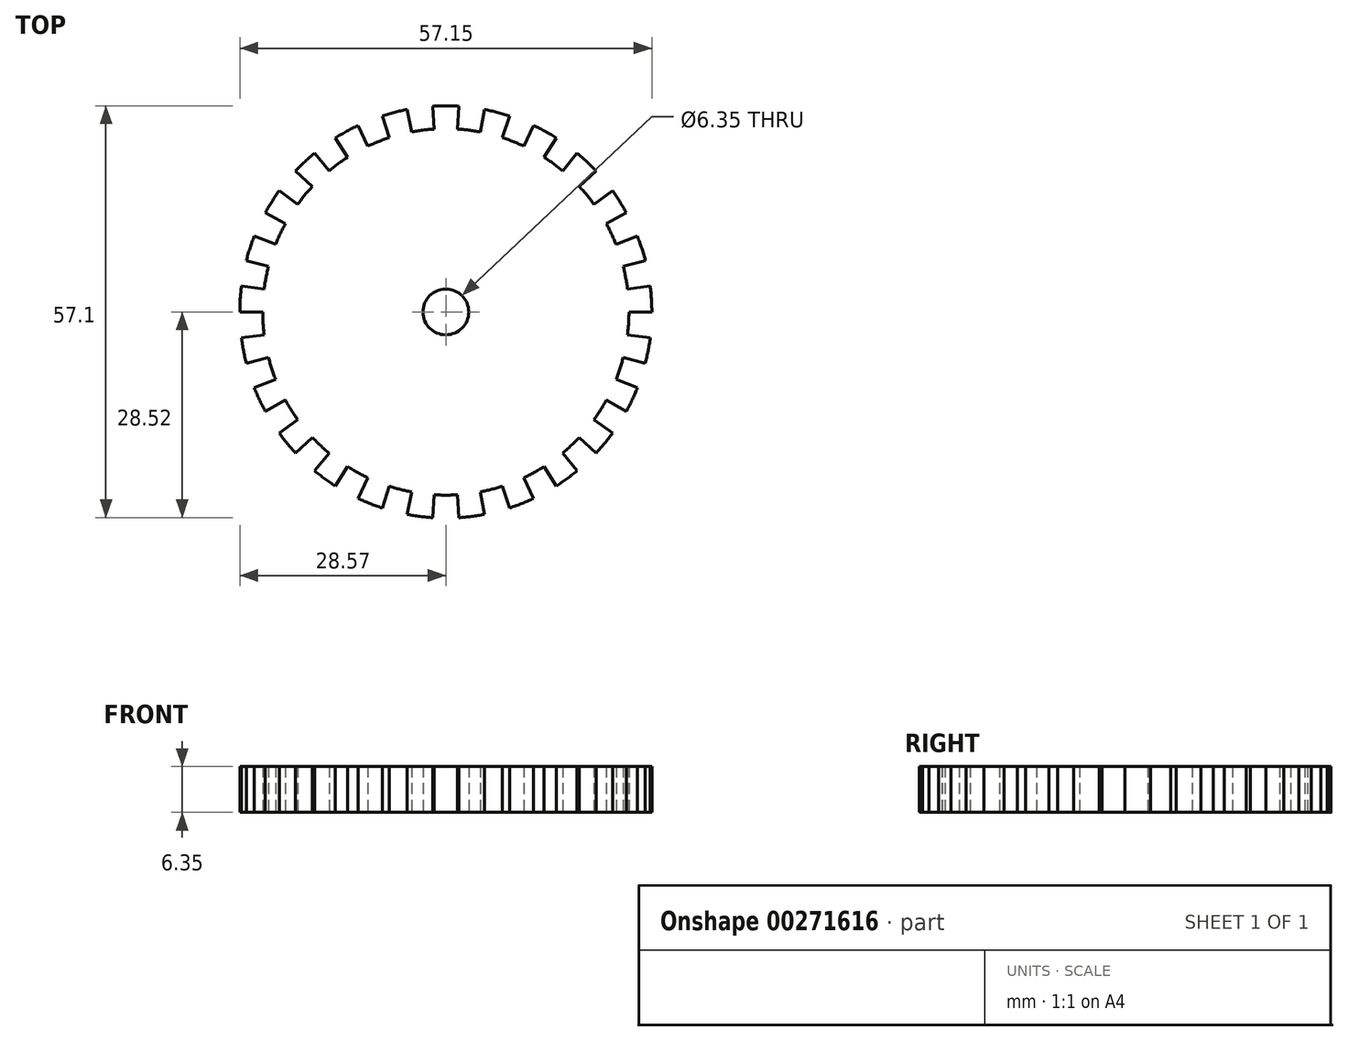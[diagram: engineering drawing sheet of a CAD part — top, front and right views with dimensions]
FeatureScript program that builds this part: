
annotation { "Feature Type Name" : "Feature", "Feature Type Description" : "" }
export const myFeature = defineFeature(function(context is Context, id is Id, definition is map)
    precondition{}
    {
        {
            var Q0;
            Q0=qCreatedBy(makeId("Top.planeOp"),FACE);
            var sketch = newSketch(context, id + "F0", { "sketchPlane" : qUnion([Q0])});
            skArc(sketch, "E0", {"start": v(-5.35, 28.07) * mm, "mid": v(-7.1, 27.68) * mm, "end": v(-8.83, 27.18) * mm});
            skArc(sketch, "E1", {"start": v(-1.6, 25.35) * mm, "mid": v(-3.18, 25.2) * mm, "end": v(-4.76, 24.95) * mm});
            skLineSegment(sketch, "E2", {"start": v(22.26, 12.24) * mm, "end": v(25.04, 13.77) * mm});
            skLineSegment(sketch, "E3", {"start": v(24.6, -6.32) * mm, "end": v(27.68, -7.1) * mm});
            skLineSegment(sketch, "E4", {"start": v(22.26, -12.24) * mm, "end": v(25.04, -13.77) * mm});
            skLineSegment(sketch, "E5", {"start": v(18.52, -17.39) * mm, "end": v(20.83, -19.56) * mm});
            skLineSegment(sketch, "E6.trimOffspring", {"start": v(1.8, -28.52) * mm, "end": v(1.6, -25.35) * mm});
            skLineSegment(sketch, "E7.trimOffspring", {"start": v(5.35, -28.07) * mm, "end": v(4.76, -24.95) * mm});
            skLineSegment(sketch, "E8.trimOffspring", {"start": v(8.83, -27.18) * mm, "end": v(7.85, -24.16) * mm});
            skLineSegment(sketch, "E9.trimOffspring", {"start": v(12.17, -25.86) * mm, "end": v(10.81, -22.98) * mm});
            skLineSegment(sketch, "E10.trimOffspring", {"start": v(15.31, -24.13) * mm, "end": v(13.61, -21.45) * mm});
            skLineSegment(sketch, "E11.trimOffspring", {"start": v(18.21, -22.02) * mm, "end": v(16.2, -19.57) * mm});
            skLineSegment(sketch, "E12.trimOffspring", {"start": v(23.12, -16.8) * mm, "end": v(20.55, -14.93) * mm});
            skLineSegment(sketch, "E13.trimOffspring", {"start": v(26.57, -10.52) * mm, "end": v(23.62, -9.35) * mm});
            skLineSegment(sketch, "E14.trimOffspring", {"start": v(28.35, -3.58) * mm, "end": v(25.2, -3.18) * mm});
            skLineSegment(sketch, "E15.trimOffspring", {"start": v(28.58, 0) * mm, "end": v(25.4, 0) * mm});
            skLineSegment(sketch, "E16.trimOffspring", {"start": v(28.35, 3.58) * mm, "end": v(25.2, 3.18) * mm});
            skLineSegment(sketch, "E17.trimOffspring", {"start": v(27.68, 7.1) * mm, "end": v(24.6, 6.32) * mm});
            skLineSegment(sketch, "E18.trimOffspring", {"start": v(26.57, 10.52) * mm, "end": v(23.62, 9.35) * mm});
            skLineSegment(sketch, "E19.trimOffspring", {"start": v(23.12, 16.8) * mm, "end": v(20.55, 14.93) * mm});
            skLineSegment(sketch, "E20.trimOffspring", {"start": v(20.83, 19.56) * mm, "end": v(18.52, 17.39) * mm});
            skLineSegment(sketch, "E21.trimOffspring", {"start": v(18.21, 22.02) * mm, "end": v(16.2, 19.57) * mm});
            skLineSegment(sketch, "E22.trimOffspring", {"start": v(15.31, 24.13) * mm, "end": v(13.61, 21.45) * mm});
            skLineSegment(sketch, "E23.trimOffspring", {"start": v(12.17, 25.86) * mm, "end": v(10.81, 22.98) * mm});
            skLineSegment(sketch, "E24.trimOffspring", {"start": v(8.83, 27.18) * mm, "end": v(7.85, 24.16) * mm});
            skLineSegment(sketch, "E25.trimOffspring", {"start": v(5.35, 28.07) * mm, "end": v(4.76, 24.95) * mm});
            skLineSegment(sketch, "E26.trimOffspring", {"start": v(1.8, 28.52) * mm, "end": v(1.6, 25.35) * mm});
            skLineSegment(sketch, "E27.trimOffspring", {"start": v(-1.8, 28.52) * mm, "end": v(-1.6, 25.35) * mm});
            skLineSegment(sketch, "E28.trimOffspring", {"start": v(-5.35, 28.07) * mm, "end": v(-4.76, 24.95) * mm});
            skArc(sketch, "E29.trimOffspring", {"start": v(1.8, 28.52) * mm, "mid": v(0, 28.58) * mm, "end": v(-1.8, 28.52) * mm});
            skArc(sketch, "E30.trimOffspring", {"start": v(4.76, 24.95) * mm, "mid": v(3.18, 25.2) * mm, "end": v(1.6, 25.35) * mm});
            skArc(sketch, "E31.trimOffspring", {"start": v(8.83, 27.18) * mm, "mid": v(7.1, 27.68) * mm, "end": v(5.35, 28.07) * mm});
            skArc(sketch, "E32.trimOffspring", {"start": v(10.81, 22.98) * mm, "mid": v(9.35, 23.62) * mm, "end": v(7.85, 24.16) * mm});
            skArc(sketch, "E33.trimOffspring", {"start": v(15.31, 24.13) * mm, "mid": v(13.77, 25.04) * mm, "end": v(12.17, 25.86) * mm});
            skArc(sketch, "E34.trimOffspring", {"start": v(16.2, 19.57) * mm, "mid": v(14.93, 20.55) * mm, "end": v(13.61, 21.45) * mm});
            skArc(sketch, "E35.trimOffspring", {"start": v(20.83, 19.56) * mm, "mid": v(19.56, 20.83) * mm, "end": v(18.21, 22.02) * mm});
            skArc(sketch, "E36.trimOffspring", {"start": v(20.55, 14.93) * mm, "mid": v(19.57, 16.2) * mm, "end": v(18.52, 17.39) * mm});
            skArc(sketch, "E37.trimOffspring", {"start": v(25.04, 13.77) * mm, "mid": v(24.13, 15.31) * mm, "end": v(23.12, 16.8) * mm});
            skArc(sketch, "E38.trimOffspring", {"start": v(23.62, 9.35) * mm, "mid": v(22.98, 10.81) * mm, "end": v(22.26, 12.24) * mm});
            skArc(sketch, "E39.trimOffspring", {"start": v(27.68, 7.1) * mm, "mid": v(27.18, 8.83) * mm, "end": v(26.57, 10.52) * mm});
            skArc(sketch, "E40.trimOffspring", {"start": v(25.2, 3.18) * mm, "mid": v(24.95, 4.76) * mm, "end": v(24.6, 6.32) * mm});
            skArc(sketch, "E41.trimOffspring", {"start": v(28.58, 0) * mm, "mid": v(28.52, 1.8) * mm, "end": v(28.35, 3.58) * mm});
            skArc(sketch, "E42.trimOffspring", {"start": v(25.2, -3.18) * mm, "mid": v(25.35, -1.6) * mm, "end": v(25.4, 0) * mm});
            skArc(sketch, "E43.trimOffspring", {"start": v(27.68, -7.1) * mm, "mid": v(28.07, -5.35) * mm, "end": v(28.35, -3.58) * mm});
            skArc(sketch, "E44.trimOffspring", {"start": v(23.62, -9.35) * mm, "mid": v(24.16, -7.85) * mm, "end": v(24.6, -6.32) * mm});
            skArc(sketch, "E45.trimOffspring", {"start": v(25.04, -13.77) * mm, "mid": v(25.86, -12.17) * mm, "end": v(26.57, -10.52) * mm});
            skArc(sketch, "E46.trimOffspring", {"start": v(20.55, -14.93) * mm, "mid": v(21.45, -13.61) * mm, "end": v(22.26, -12.24) * mm});
            skArc(sketch, "E47.trimOffspring", {"start": v(20.83, -19.56) * mm, "mid": v(22.02, -18.21) * mm, "end": v(23.12, -16.8) * mm});
            skArc(sketch, "E48.trimOffspring", {"start": v(16.2, -19.57) * mm, "mid": v(17.39, -18.52) * mm, "end": v(18.52, -17.39) * mm});
            skArc(sketch, "E49.trimOffspring", {"start": v(15.31, -24.13) * mm, "mid": v(16.8, -23.12) * mm, "end": v(18.21, -22.02) * mm});
            skArc(sketch, "E50.trimOffspring", {"start": v(10.81, -22.98) * mm, "mid": v(12.24, -22.26) * mm, "end": v(13.61, -21.45) * mm});
            skArc(sketch, "E51.trimOffspring", {"start": v(8.83, -27.18) * mm, "mid": v(10.52, -26.57) * mm, "end": v(12.17, -25.86) * mm});
            skArc(sketch, "E52.trimOffspring", {"start": v(4.76, -24.95) * mm, "mid": v(6.32, -24.6) * mm, "end": v(7.85, -24.16) * mm});
            skArc(sketch, "E53.MirrorCS", {"start": v(-20.55, 14.93) * mm, "mid": v(-19.57, 16.2) * mm, "end": v(-18.52, 17.39) * mm});
            skLineSegment(sketch, "E54.MirrorCS", {"start": v(-28.35, -3.58) * mm, "end": v(-25.2, -3.18) * mm});
            skLineSegment(sketch, "E55.MirrorCS", {"start": v(-12.17, 25.86) * mm, "end": v(-10.81, 22.98) * mm});
            skLineSegment(sketch, "E56.MirrorCS", {"start": v(-23.12, -16.8) * mm, "end": v(-20.55, -14.93) * mm});
            skLineSegment(sketch, "E57.MirrorCS", {"start": v(-22.26, -12.24) * mm, "end": v(-25.04, -13.77) * mm});
            skLineSegment(sketch, "E58.MirrorCS", {"start": v(-28.58, 0) * mm, "end": v(-25.4, 0) * mm});
            skArc(sketch, "E59.MirrorCS", {"start": v(-27.68, 7.1) * mm, "mid": v(-27.18, 8.83) * mm, "end": v(-26.57, 10.52) * mm});
            skArc(sketch, "E60.MirrorCS", {"start": v(-20.55, -14.93) * mm, "mid": v(-21.45, -13.61) * mm, "end": v(-22.26, -12.24) * mm});
            skLineSegment(sketch, "E61.MirrorCS", {"start": v(-15.31, -24.13) * mm, "end": v(-13.61, -21.45) * mm});
            skLineSegment(sketch, "E62.MirrorCS", {"start": v(-5.35, -28.07) * mm, "end": v(-4.76, -24.95) * mm});
            skArc(sketch, "E63.MirrorCS", {"start": v(-16.2, -19.57) * mm, "mid": v(-17.39, -18.52) * mm, "end": v(-18.52, -17.39) * mm});
            skLineSegment(sketch, "E64.MirrorCS", {"start": v(-23.12, 16.8) * mm, "end": v(-20.55, 14.93) * mm});
            skArc(sketch, "E65.MirrorCS", {"start": v(-20.83, -19.56) * mm, "mid": v(-22.02, -18.21) * mm, "end": v(-23.12, -16.8) * mm});
            skLineSegment(sketch, "E66.MirrorCS", {"start": v(-18.21, -22.02) * mm, "end": v(-16.2, -19.57) * mm});
            skArc(sketch, "E67.MirrorCS", {"start": v(-27.68, -7.1) * mm, "mid": v(-28.07, -5.35) * mm, "end": v(-28.35, -3.58) * mm});
            skArc(sketch, "E68.MirrorCS", {"start": v(-23.62, -9.35) * mm, "mid": v(-24.16, -7.85) * mm, "end": v(-24.6, -6.32) * mm});
            skLineSegment(sketch, "E69.MirrorCS", {"start": v(-18.52, -17.39) * mm, "end": v(-20.83, -19.56) * mm});
            skArc(sketch, "E70.MirrorCS", {"start": v(-15.31, -24.13) * mm, "mid": v(-16.8, -23.12) * mm, "end": v(-18.21, -22.02) * mm});
            skLineSegment(sketch, "E71.MirrorCS", {"start": v(-27.68, 7.1) * mm, "end": v(-24.6, 6.32) * mm});
            skArc(sketch, "E72.MirrorCS", {"start": v(-25.2, 3.18) * mm, "mid": v(-24.95, 4.76) * mm, "end": v(-24.6, 6.32) * mm});
            skLineSegment(sketch, "E73.MirrorCS", {"start": v(-22.26, 12.24) * mm, "end": v(-25.04, 13.77) * mm});
            skLineSegment(sketch, "E74.MirrorCS", {"start": v(-8.83, -27.18) * mm, "end": v(-7.85, -24.16) * mm});
            skArc(sketch, "E75.MirrorCS", {"start": v(-25.2, -3.18) * mm, "mid": v(-25.35, -1.6) * mm, "end": v(-25.4, 0) * mm});
            skArc(sketch, "E76.MirrorCS", {"start": v(-20.83, 19.56) * mm, "mid": v(-19.56, 20.83) * mm, "end": v(-18.21, 22.02) * mm});
            skLineSegment(sketch, "E77.MirrorCS", {"start": v(-18.21, 22.02) * mm, "end": v(-16.2, 19.57) * mm});
            skLineSegment(sketch, "E78.MirrorCS", {"start": v(-20.83, 19.56) * mm, "end": v(-18.52, 17.39) * mm});
            skArc(sketch, "E79.MirrorCS", {"start": v(-8.83, -27.18) * mm, "mid": v(-10.52, -26.57) * mm, "end": v(-12.17, -25.86) * mm});
            skArc(sketch, "E80.MirrorCS", {"start": v(-8.83, 27.18) * mm, "mid": v(-7.1, 27.68) * mm, "end": v(-5.35, 28.07) * mm});
            skArc(sketch, "E81.MirrorCS", {"start": v(-4.76, -24.95) * mm, "mid": v(-6.32, -24.6) * mm, "end": v(-7.85, -24.16) * mm});
            skArc(sketch, "E82.MirrorCS", {"start": v(-10.81, -22.98) * mm, "mid": v(-12.24, -22.26) * mm, "end": v(-13.61, -21.45) * mm});
            skLineSegment(sketch, "E83.MirrorCS", {"start": v(-15.31, 24.13) * mm, "end": v(-13.61, 21.45) * mm});
            skLineSegment(sketch, "E84.MirrorCS", {"start": v(-26.57, 10.52) * mm, "end": v(-23.62, 9.35) * mm});
            skLineSegment(sketch, "E85.MirrorCS", {"start": v(-12.17, -25.86) * mm, "end": v(-10.81, -22.98) * mm});
            skArc(sketch, "E86.MirrorCS", {"start": v(-15.31, 24.13) * mm, "mid": v(-13.77, 25.04) * mm, "end": v(-12.17, 25.86) * mm});
            skLineSegment(sketch, "E87.MirrorCS", {"start": v(-8.83, 27.18) * mm, "end": v(-7.85, 24.16) * mm});
            skArc(sketch, "E88.MirrorCS", {"start": v(-16.2, 19.57) * mm, "mid": v(-14.93, 20.55) * mm, "end": v(-13.61, 21.45) * mm});
            skArc(sketch, "E89.MirrorCS", {"start": v(-25.04, 13.77) * mm, "mid": v(-24.13, 15.31) * mm, "end": v(-23.12, 16.8) * mm});
            skArc(sketch, "E90.MirrorCS", {"start": v(-23.62, 9.35) * mm, "mid": v(-22.98, 10.81) * mm, "end": v(-22.26, 12.24) * mm});
            skLineSegment(sketch, "E91.MirrorCS", {"start": v(-24.6, -6.32) * mm, "end": v(-27.68, -7.1) * mm});
            skArc(sketch, "E92.MirrorCS", {"start": v(-28.58, 0) * mm, "mid": v(-28.52, 1.8) * mm, "end": v(-28.35, 3.58) * mm});
            skArc(sketch, "E93.MirrorCS", {"start": v(-25.04, -13.77) * mm, "mid": v(-25.86, -12.17) * mm, "end": v(-26.57, -10.52) * mm});
            skLineSegment(sketch, "E94.MirrorCS", {"start": v(-26.57, -10.52) * mm, "end": v(-23.62, -9.35) * mm});
            skArc(sketch, "E95.MirrorCS", {"start": v(-10.81, 22.98) * mm, "mid": v(-9.35, 23.62) * mm, "end": v(-7.85, 24.16) * mm});
            skLineSegment(sketch, "E96.MirrorCS", {"start": v(-28.35, 3.58) * mm, "end": v(-25.2, 3.18) * mm});
            skLineSegment(sketch, "E97.MirrorCS", {"start": v(-1.8, -28.52) * mm, "end": v(-1.6, -25.35) * mm});
            skArc(sketch, "E98.trimOffspring", {"start": v(1.8, -28.52) * mm, "mid": v(3.58, -28.35) * mm, "end": v(5.35, -28.07) * mm});
            skArc(sketch, "E99.trimOffspring", {"start": v(-1.6, -25.35) * mm, "mid": v(0, -25.4) * mm, "end": v(1.6, -25.35) * mm});
            skArc(sketch, "E100.trimOffspring", {"start": v(-5.35, -28.07) * mm, "mid": v(-3.58, -28.35) * mm, "end": v(-1.8, -28.52) * mm});
            skArc(sketch, "E101.trimOffspring", {"start": v(-7.85, -24.16) * mm, "mid": v(-6.32, -24.6) * mm, "end": v(-4.76, -24.95) * mm});
            skArc(sketch, "E102.trimOffspring", {"start": v(-12.17, -25.86) * mm, "mid": v(-10.52, -26.57) * mm, "end": v(-8.83, -27.18) * mm});
            skArc(sketch, "E103.trimOffspring", {"start": v(-13.61, -21.45) * mm, "mid": v(-12.24, -22.26) * mm, "end": v(-10.81, -22.98) * mm});
            skArc(sketch, "E104.trimOffspring", {"start": v(-18.21, -22.02) * mm, "mid": v(-16.8, -23.12) * mm, "end": v(-15.31, -24.13) * mm});
            skArc(sketch, "E105.trimOffspring", {"start": v(-18.52, -17.39) * mm, "mid": v(-17.39, -18.52) * mm, "end": v(-16.2, -19.57) * mm});
            skArc(sketch, "E106.trimOffspring", {"start": v(-23.12, -16.8) * mm, "mid": v(-22.02, -18.21) * mm, "end": v(-20.83, -19.56) * mm});
            skArc(sketch, "E107.trimOffspring", {"start": v(-22.26, -12.24) * mm, "mid": v(-21.45, -13.61) * mm, "end": v(-20.55, -14.93) * mm});
            skArc(sketch, "E108.trimOffspring", {"start": v(-26.57, -10.52) * mm, "mid": v(-25.86, -12.17) * mm, "end": v(-25.04, -13.77) * mm});
            skArc(sketch, "E109.trimOffspring", {"start": v(-24.6, -6.32) * mm, "mid": v(-24.16, -7.85) * mm, "end": v(-23.62, -9.35) * mm});
            skArc(sketch, "E110.trimOffspring", {"start": v(-28.35, -3.58) * mm, "mid": v(-28.07, -5.35) * mm, "end": v(-27.68, -7.1) * mm});
            skArc(sketch, "E111.trimOffspring", {"start": v(-25.4, 0) * mm, "mid": v(-25.35, -1.6) * mm, "end": v(-25.2, -3.18) * mm});
            skArc(sketch, "E112.trimOffspring", {"start": v(-28.35, 3.58) * mm, "mid": v(-28.52, 1.8) * mm, "end": v(-28.58, 0) * mm});
            skArc(sketch, "E113.trimOffspring", {"start": v(-24.6, 6.32) * mm, "mid": v(-24.95, 4.76) * mm, "end": v(-25.2, 3.18) * mm});
            skArc(sketch, "E114.trimOffspring", {"start": v(-26.57, 10.52) * mm, "mid": v(-27.18, 8.83) * mm, "end": v(-27.68, 7.1) * mm});
            skArc(sketch, "E115.trimOffspring", {"start": v(-22.26, 12.24) * mm, "mid": v(-22.98, 10.81) * mm, "end": v(-23.62, 9.35) * mm});
            skArc(sketch, "E116.trimOffspring", {"start": v(-23.12, 16.8) * mm, "mid": v(-24.13, 15.31) * mm, "end": v(-25.04, 13.77) * mm});
            skArc(sketch, "E117.trimOffspring", {"start": v(-18.52, 17.39) * mm, "mid": v(-19.57, 16.2) * mm, "end": v(-20.55, 14.93) * mm});
            skArc(sketch, "E118.trimOffspring", {"start": v(-18.21, 22.02) * mm, "mid": v(-19.56, 20.83) * mm, "end": v(-20.83, 19.56) * mm});
            skArc(sketch, "E119.trimOffspring", {"start": v(-13.61, 21.45) * mm, "mid": v(-14.93, 20.55) * mm, "end": v(-16.2, 19.57) * mm});
            skArc(sketch, "E120.trimOffspring", {"start": v(-7.85, 24.16) * mm, "mid": v(-9.35, 23.62) * mm, "end": v(-10.81, 22.98) * mm});
            skArc(sketch, "E121.trimOffspring", {"start": v(-12.17, 25.86) * mm, "mid": v(-13.77, 25.04) * mm, "end": v(-15.31, 24.13) * mm});
            skCircle(sketch, "E122", {"center": v(0, 0) * mm, "radius": 3.18 * mm});
            skSolve(sketch);
        }
        {
            var Q0;
            Q0=makeQuery(id+"F0.imprint","IMPRINT",FACE,{"disambiguationData":[TD([[makeQuery(id+"F0.imprint","IMPRINT",EDGE,{"derivedFrom":sQuery(id+"F0.wireOp",EDGE,"E0")}),1.0]])]});
            extrude(context, id + "F1", {"entities" : qUnion([Q0]), "depth" : 6.35 * mm, "offsetDistance" : 25.4 * mm});
        }
    });
